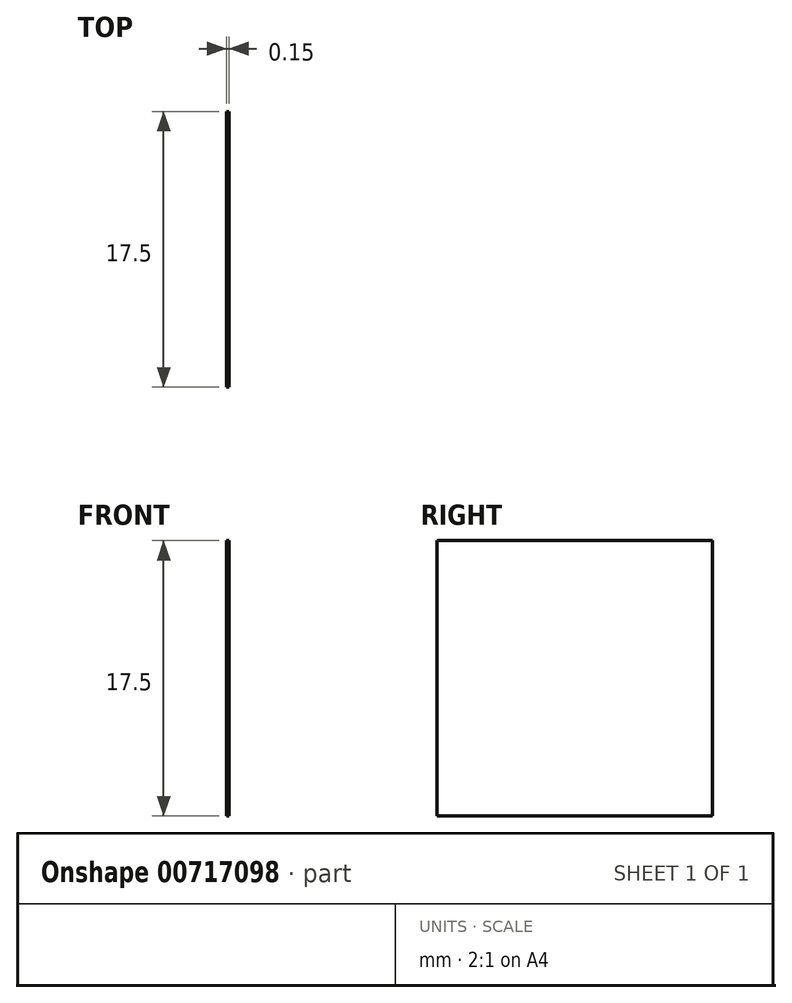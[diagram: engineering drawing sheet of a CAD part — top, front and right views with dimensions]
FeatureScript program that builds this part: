
annotation { "Feature Type Name" : "Feature", "Feature Type Description" : "" }
export const myFeature = defineFeature(function(context is Context, id is Id, definition is map)
    precondition{}
    {
        {
            var Q0;
            Q0=qCreatedBy(makeId("Right.planeOp"),FACE);
            var sketch = newSketch(context, id + "F0", { "sketchPlane" : qUnion([Q0])});
            skLineSegment(sketch, "E0.bottom", {"start": v(0, 0) * mm, "end": v(17.5, 0) * mm});
            skLineSegment(sketch, "E0.top", {"start": v(0, -17.5) * mm, "end": v(17.5, -17.5) * mm});
            skLineSegment(sketch, "E0.left", {"start": v(0, 0) * mm, "end": v(0, -17.5) * mm});
            skLineSegment(sketch, "E0.right", {"start": v(17.5, 0) * mm, "end": v(17.5, -17.5) * mm});
            skSolve(sketch);
        }
        {
            var Q0;
            Q0=makeQuery(id+"F0.imprint","IMPRINT",FACE,{"disambiguationData":[TD([[makeQuery(id+"F0.imprint","IMPRINT",EDGE,{"derivedFrom":sQuery(id+"F0.wireOp",EDGE,"E0.bottom")}),-1.0]])]});
            extrude(context, id + "F1", {"entities" : qUnion([Q0]), "depth" : .15 * mm, "offsetDistance" : 25 * mm});
        }
    });
